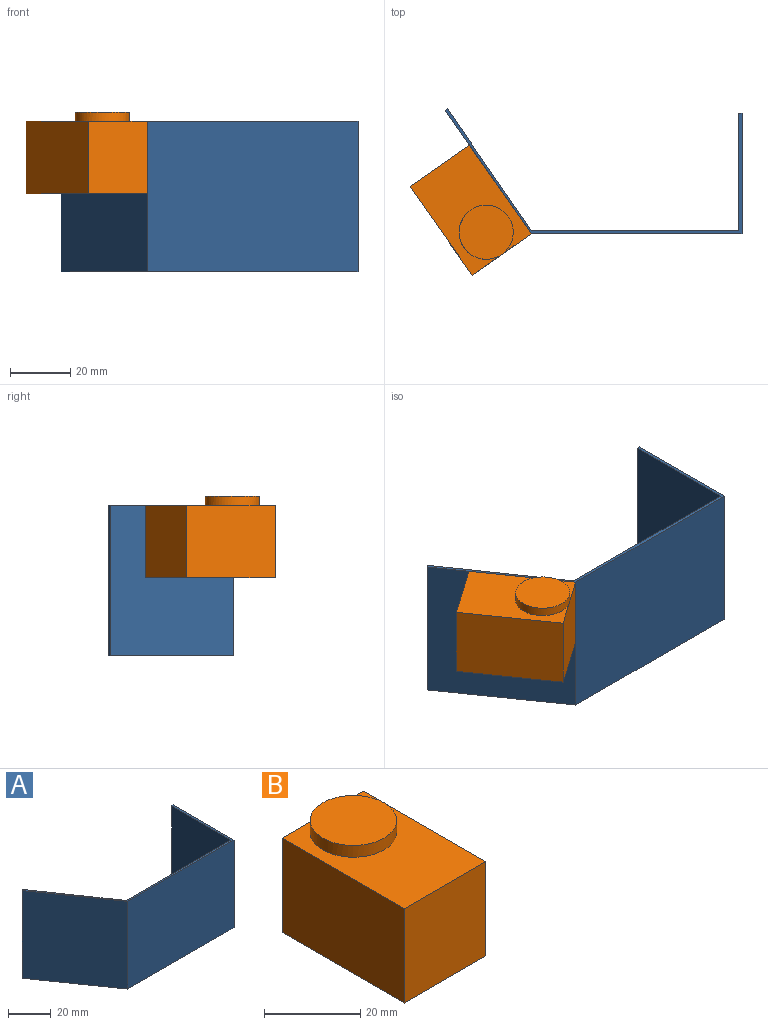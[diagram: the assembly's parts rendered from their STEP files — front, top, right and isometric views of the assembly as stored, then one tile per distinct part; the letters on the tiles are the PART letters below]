
ASSEMBLY  parts=2 mates=1
PART A: 10 faces, bbox 98.7x41.5x50 mm
  f0: plane 70x50mm, normal (0,-1,0), area 3500mm2, adj f1,f7,f8,f9
  f1: plane 50x40mm, normal (1,0,0), area 2000mm2, adj f0,f2,f8,f9
  f2: plane 50x1mm, normal (0,1,0), area 50mm2, adj f1,f3,f8,f9
  f3: plane 50x39mm, normal (-1,0,0), area 1950mm2, adj f2,f4,f8,f9
  f4: plane 69x50mm, normal (0,1,0), area 3450mm2, adj f3,f5,f8,f9
  f5: plane 50x40.53mm, normal (0.82,0.57,0), area 2459.1mm2, adj f4,f6,f8,f9
  f6: plane 50x0.82mm, normal (-0.57,0.82,0), area 50mm2, adj f5,f7,f8,f9
  f7: plane 50x40.96mm, normal (-0.82,-0.57,0), area 2500mm2, adj f0,f6,f8,f9
  f8: plane 98.68x41.53mm, normal (0,0,1), area 147.9mm2, adj f0,f1,f2,f3,f4,f5,f6,f7
  f9: plane 98.68x41.53mm, normal (0,0,-1), area 147.9mm2, adj f0,f1,f2,f3,f4,f5,f6,f7
PART B: 8 faces, bbox 24x36x27 mm
  f0: cylinder r=9mm len=18mm, axis (0,0,-1), area 169.6mm2, adj f1,f2
  f1: plane 18x18mm, normal (0,0,1), area 254.5mm2, adj f0
  f2: plane 36x24mm, normal (0,0,1), area 609.5mm2, adj f0,f3,f4,f5,f6
  f3: plane 24x24mm, normal (0,1,0), area 576mm2, adj f2,f4,f6,f7
  f4: plane 36x24mm, normal (-1,0,0), area 864mm2, adj f2,f3,f5,f7
  f5: plane 24x24mm, normal (0,-1,0), area 576mm2, adj f2,f4,f6,f7
  f6: plane 36x24mm, normal (1,0,0), area 864mm2, adj f2,f3,f5,f7
  f7: plane 36x24mm, normal (0,0,-1), area 864mm2, adj f3,f4,f5,f6
PLACE A t=(-14.39,-8.35,-1.36)mm
PLACE B rot(axis=(0,0,-1),145deg) t=(-36.27,4.26,48.64)mm
MATE fastened A.f7 <-> B.f4  axis (-0.82,-0.57,0) through (-28.73,12.13,23.64)mm
